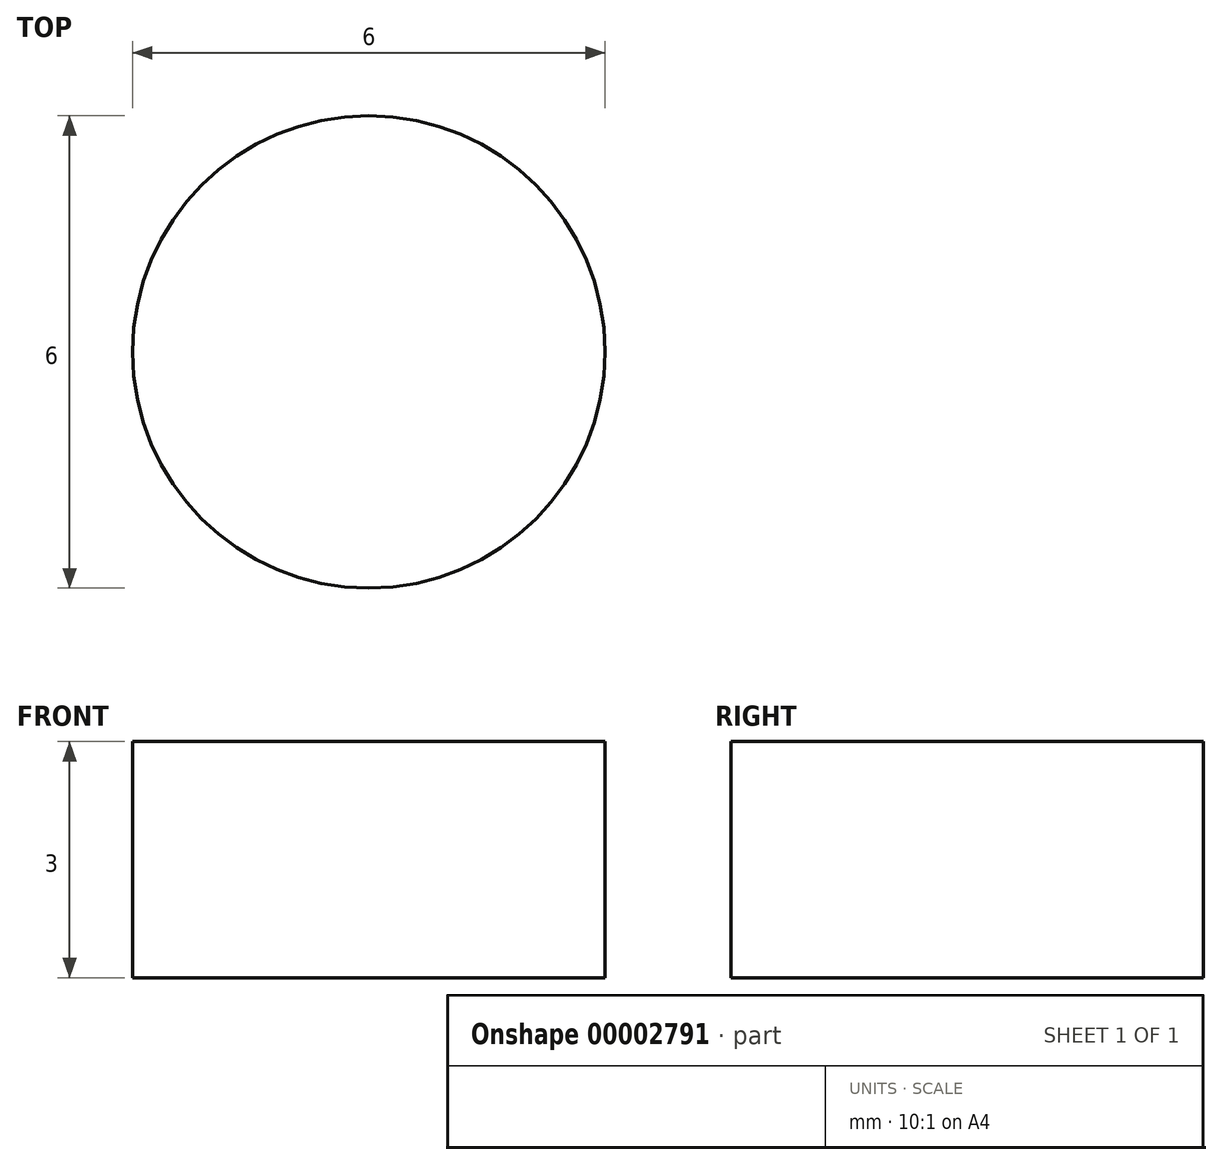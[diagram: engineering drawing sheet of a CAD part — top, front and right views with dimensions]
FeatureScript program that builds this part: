
annotation { "Feature Type Name" : "Feature", "Feature Type Description" : "" }
export const myFeature = defineFeature(function(context is Context, id is Id, definition is map)
    precondition{}
    {
        {
            var Q0;
            Q0=qCreatedBy(makeId("Front.planeOp"),FACE);
            var sketch = newSketch(context, id + "F0", { "sketchPlane" : qUnion([Q0])});
            skLineSegment(sketch, "E0", {"start": v(0, 0) * mm, "end": v(-7.55, 0) * mm, "construction": true});
            skLineSegment(sketch, "E1.0", {"start": v(-3.25, 4) * mm, "end": v(-3.25, 1) * mm});
            skLineSegment(sketch, "E2", {"start": v(0, 0) * mm, "end": v(-7.55, 0) * mm});
            skLineSegment(sketch, "E3.0", {"start": v(-3.25, 4) * mm, "end": v(-3.75, 4) * mm});
            skLineSegment(sketch, "E4.0", {"start": v(-6.25, 6) * mm, "end": v(-7.55, 0) * mm});
            skLineSegment(sketch, "E5.0", {"start": v(0, 1) * mm, "end": v(-3.25, 1) * mm});
            skLineSegment(sketch, "E6", {"start": v(-5.25, 6) * mm, "end": v(-3.75, 4) * mm});
            skLineSegment(sketch, "E7.trimOffspring", {"start": v(-5.25, 6) * mm, "end": v(-6.25, 6) * mm});
            skLineSegment(sketch, "E8", {"start": v(0, 0) * mm, "end": v(0, 1) * mm});
            skSolve(sketch);
        }
        {
            var Q0;
            Q0=makeQuery(id+"F0.imprint","IMPRINT",FACE,{"disambiguationData":[TD([[makeQuery(id+"F0.imprint","IMPRINT",EDGE,{"derivedFrom":sQuery(id+"F0.wireOp",EDGE,"E1.0")}),-1.0]])]});
            var Q1;
            Q1=sQuery(id+"F0.wireOp",EDGE,"E8");
            revolve(context, id + "F1", {"entities" : qUnion([Q0]), "axis" : qUnion([Q1]), "revolveType" : RevolveType.FULL});
        }
        {
            var Q0;
            Q0=makeQuery(id+"F1.opRevolve","SWEPT_FACE",FACE,{"disambiguationData":[OSD([sQuery(id+"F0.wireOp",EDGE,"E5.0")])]});
            var sketch = newSketch(context, id + "F2", { "sketchPlane" : qUnion([Q0])});
            skCircle(sketch, "E9", {"center": v(0, 0) * mm, "radius": 3 * mm});
            skSolve(sketch);
        }
        {
            var Q0;
            Q0=qSketchRegion(id+"F2",true);
            extrude(context, id + "F3", {"entities" : qUnion([Q0]), "depth" : 3 * mm});
        }
        {
            var Q0;
            Q0=makeQuery(id+"F1.opRevolve","SWEPT_BODY",BODY,{"disambiguationData":[OSD([sQuery(id+"F0.wireOp",EDGE,"E1.0"),sQuery(id+"F0.wireOp",EDGE,"E2"),sQuery(id+"F0.wireOp",EDGE,"E3.0"),sQuery(id+"F0.wireOp",EDGE,"E4.0"),sQuery(id+"F0.wireOp",EDGE,"E5.0"),sQuery(id+"F0.wireOp",EDGE,"E6"),sQuery(id+"F0.wireOp",EDGE,"E7.trimOffspring"),sQuery(id+"F0.wireOp",EDGE,"E8")])]});
            deleteBodies(context, id + "F4", {"entities" : qUnion([Q0])});
        }
    });
